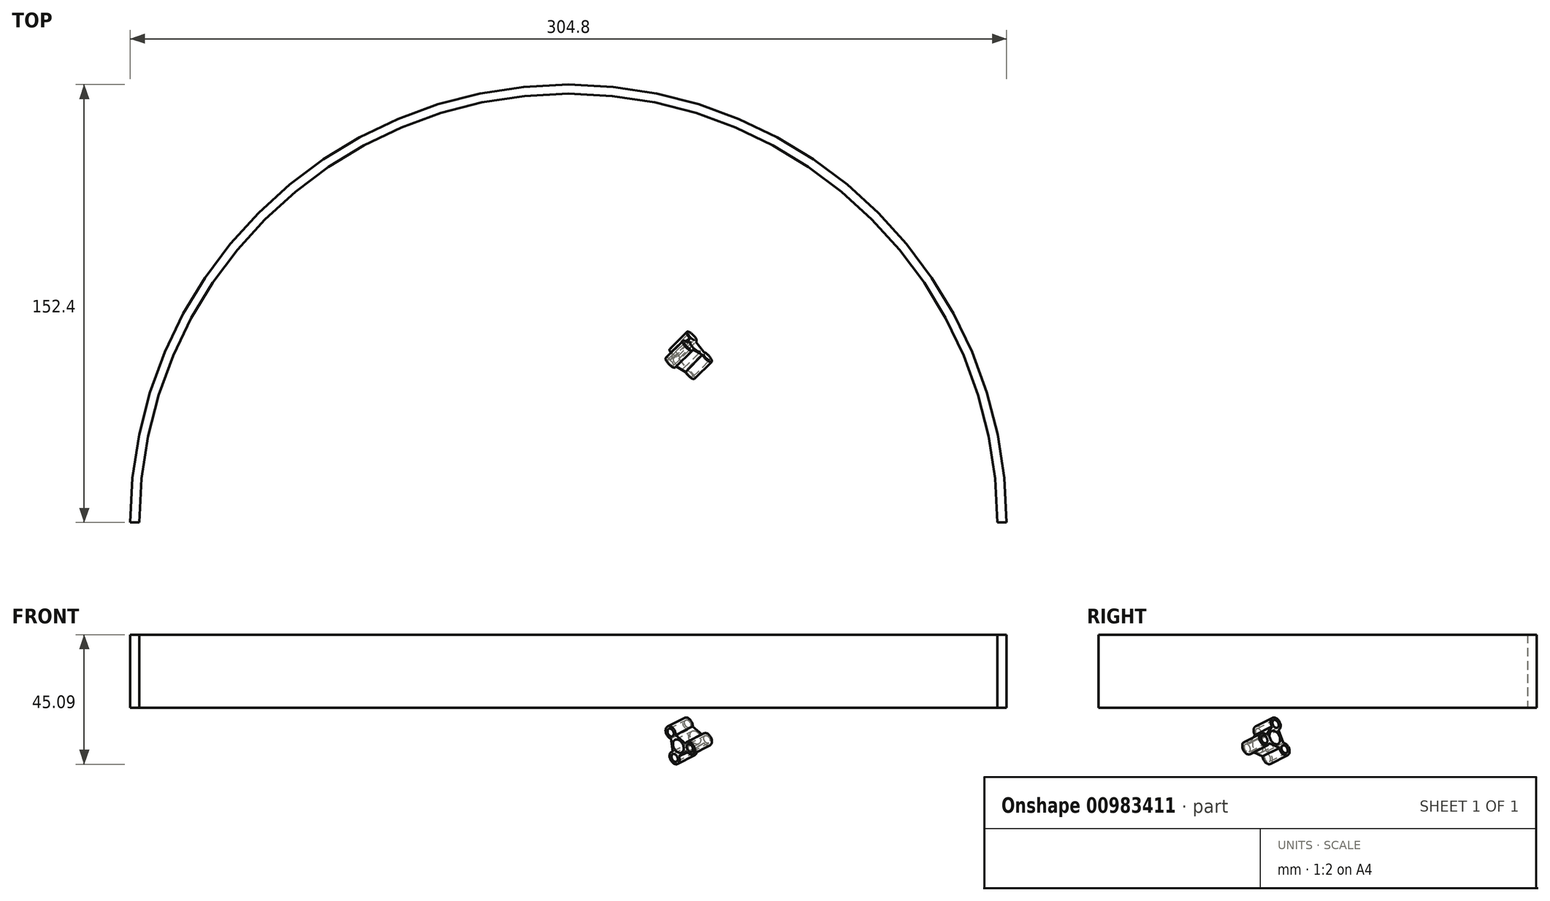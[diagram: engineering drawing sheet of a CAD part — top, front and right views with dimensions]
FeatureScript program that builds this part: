
annotation { "Feature Type Name" : "Feature", "Feature Type Description" : "" }
export const myFeature = defineFeature(function(context is Context, id is Id, definition is map)
    precondition{}
    {
        {
            var Q0;
            Q0=qCreatedBy(makeId("Top.planeOp"),FACE);
            var sketch = newSketch(context, id + "F0", { "sketchPlane" : qUnion([Q0])});
            skArc(sketch, "E0", {"start": v(139.7, 0) * mm, "mid": v(0, 139.7) * mm, "end": v(-139.7, 0) * mm, "construction": true});
            skArc(sketch, "E1", {"start": v(152.4, 0) * mm, "mid": v(0, 152.4) * mm, "end": v(-152.4, 0) * mm});
            skLineSegment(sketch, "E2", {"start": v(0, 0) * mm, "end": v(-209.94, 0) * mm, "construction": true});
            skLineSegment(sketch, "E3", {"start": v(0, 0) * mm, "end": v(212.99, 0) * mm, "construction": true});
            skArc(sketch, "E4.0", {"start": v(15.22, 0.84) * mm, "mid": v(0, 15.24) * mm, "end": v(-15.22, 0.84) * mm, "construction": true});
            skCircle(sketch, "E5.cCircle", {"center": v(0, 0) * mm, "radius": 12.07 * mm, "construction": true});
            skLineSegment(sketch, "E5.0", {"start": v(0, 12.06) * mm, "end": v(10.45, -6.03) * mm, "construction": true});
            skLineSegment(sketch, "E5.1", {"start": v(10.45, -6.03) * mm, "end": v(-10.45, -6.03) * mm, "construction": true});
            skLineSegment(sketch, "E5.2", {"start": v(-10.45, -6.03) * mm, "end": v(0, 12.07) * mm, "construction": true});
            skCircle(sketch, "E6", {"center": v(0, 12.07) * mm, "radius": 2.38 * mm, "construction": true});
            skCircle(sketch, "E7.1.0", {"center": v(10.45, -6.03) * mm, "radius": 2.38 * mm, "construction": true});
            skCircle(sketch, "E7.2.0", {"center": v(-10.45, -6.03) * mm, "radius": 2.38 * mm, "construction": true});
            skLineSegment(sketch, "E7.anchor2", {"start": v(0, 0) * mm, "end": v(-10.45, -6.03) * mm, "construction": true});
            skLineSegment(sketch, "E8", {"start": v(-2.92, 18.85) * mm, "end": v(-236.4, 252.33) * mm, "construction": true});
            skLineSegment(sketch, "E9.MirrorCS", {"start": v(2.92, 18.85) * mm, "end": v(-2.92, 18.85) * mm, "construction": true});
            skLineSegment(sketch, "E10.MirrorCS", {"start": v(2.92, 18.85) * mm, "end": v(236.4, 252.33) * mm, "construction": true});
            skLineSegment(sketch, "E11", {"start": v(0, 0) * mm, "end": v(0, 38.63) * mm, "construction": true});
            skArc(sketch, "E12", {"start": v(149.23, 0) * mm, "mid": v(0, 149.23) * mm, "end": v(-149.23, 0) * mm});
            skLineSegment(sketch, "E13", {"start": v(-152.4, 0) * mm, "end": v(-149.23, 0) * mm});
            skLineSegment(sketch, "E14", {"start": v(149.23, 0) * mm, "end": v(152.4, 0) * mm});
            skSolve(sketch);
        }
        {
            var Q0;
            Q0=makeQuery(id+"F0.imprint","IMPRINT",FACE,{"disambiguationData":[TD([[makeQuery(id+"F0.imprint","IMPRINT",EDGE,{"derivedFrom":sQuery(id+"F0.wireOp",EDGE,"E1")}),1.0]])]});
            extrude(context, id + "F1", {"entities" : qUnion([Q0]), "depth" : 25.4 * mm, "offsetDistance" : 25.4 * mm});
        }
        {
            var Q0;
            Q0=qCreatedBy(makeId("Top.planeOp"),FACE);
            var Q1;
            Q1=sQuery(id+"F0.wireOp",EDGE,"E9.MirrorCS");
            cPlane(context, id + "F2", {"entities" : qUnion([Q0, Q1]), "cplaneType" : CPlaneType.LINE_ANGLE, "offset" : 25.4 * mm, "angle" : 27 * degree, "oppositeDirection" : true, "width" : 152.4 * mm, "height" : 152.4 * mm});
        }
        {
            var Q0;
            Q0=makeQuery(id+"F1.opExtrude","SWEPT_BODY",BODY,{"disambiguationData":[OSD([sQuery(id+"F0.wireOp",EDGE,"E1"),sQuery(id+"F0.wireOp",EDGE,"E12"),sQuery(id+"F0.wireOp",EDGE,"E13"),sQuery(id+"F0.wireOp",EDGE,"E14")])]});
            var Q1;
            Q1=makeQuery(id+"F1.opExtrude","SWEPT_FACE",FACE,{"disambiguationData":[OSD([sQuery(id+"F0.wireOp",EDGE,"E1")])]});
            transform(context, id + "F3", {"entities" : qUnion([Q0]), "transformType" : TransformType.TRANSLATION_DISTANCE, "transformDirection" : qUnion([Q1]), "distance" : 40.13 * mm, "oppositeDirection" : true, "makeCopy" : false});
        }
        {
            var Q0;
            Q0=sQuery(id+"F0.wireOp",EDGE,"E10.MirrorCS");
            cPlane(context, id + "F4", {"entities" : qUnion([Q0]), "cplaneType" : CPlaneType.LINE_ANGLE, "offset" : 25.4 * mm, "angle" : 90 * degree, "width" : 152.4 * mm, "height" : 152.4 * mm});
        }
        {
            var Q0;
            Q0=qCreatedBy(id+"F2.planeOp",FACE);
            var sketch = newSketch(context, id + "F5", { "sketchPlane" : qUnion([Q0])});
            skLineSegment(sketch, "E15", {"start": v(48.51, -67.96) * mm, "end": v(101.32, -127.23) * mm, "construction": true});
            skSolve(sketch);
        }
        {
            var Q0;
            Q0=sQuery(id+"F5.wireOp",VERTEX,"E15.start");
            var Q1;
            Q1=sQuery(id+"F5.wireOp",EDGE,"E15");
            cPlane(context, id + "F6", {"entities" : qUnion([Q0, Q1]), "cplaneType" : CPlaneType.LINE_POINT, "offset" : 25.4 * mm, "width" : 152.4 * mm, "height" : 152.4 * mm});
        }
        {
            var Q0;
            Q0=qCreatedBy(id+"F6.planeOp",FACE);
            var sketch = newSketch(context, id + "F7", { "sketchPlane" : qUnion([Q0])});
            skCircle(sketch, "E16", {"center": v(14.1, -6.5) * mm, "radius": 2.35 * mm});
            skCircle(sketch, "E17.1.0", {"center": v(15.94, 2.78) * mm, "radius": 2.35 * mm});
            skCircle(sketch, "E17.2.0", {"center": v(6.98, -0.26) * mm, "radius": 2.35 * mm});
            skPoint(sketch, "E17.center", {"position": v(12.34, -1.33) * mm});
            skPoint(sketch, "E18.end.orphan", {"position": v(13.29, -4.3) * mm});
            skPoint(sketch, "E19.start.orphan", {"position": v(15.57, 4.29) * mm});
            skCircle(sketch, "E20", {"center": v(12.34, -1.33) * mm, "radius": 2.49 * mm});
            skCircle(sketch, "E21", {"center": v(14.1, -6.5) * mm, "radius": 1.46 * mm});
            skCircle(sketch, "E22.1.0", {"center": v(15.94, 2.78) * mm, "radius": 1.46 * mm});
            skCircle(sketch, "E22.2.0", {"center": v(6.99, -0.26) * mm, "radius": 1.46 * mm});
            skCircle(sketch, "E23.cCircle", {"center": v(12.34, -1.33) * mm, "radius": 3.18 * mm, "construction": true});
            skPoint(sketch, "E23.0.midPoint", {"position": v(11.25, 1.66) * mm});
            skLineSegment(sketch, "E24", {"start": v(13.6, 2.51) * mm, "end": v(9.05, 0.86) * mm});
            skLineSegment(sketch, "E25", {"start": v(15.03, -4.34) * mm, "end": v(15.87, 0.43) * mm});
            skLineSegment(sketch, "E26", {"start": v(12.1, -5.26) * mm, "end": v(8.38, -2.15) * mm});
            skLineSegment(sketch, "E27", {"start": v(12.34, -1.33) * mm, "end": v(14.88, -8.83) * mm, "construction": true});
            skLineSegment(sketch, "E28.0", {"start": v(7.3, -0.02) * mm, "end": v(7.3, -0.02) * mm});
            skLineSegment(sketch, "E28.1", {"start": v(12.34, -1.33) * mm, "end": v(14.1, -6.5) * mm, "construction": true});
            skLineSegment(sketch, "E28.8", {"start": v(7.3, -0.02) * mm, "end": v(7.3, -0.02) * mm});
            skLineSegment(sketch, "E28.9", {"start": v(12.23, -1.37) * mm, "end": v(14.1, -6.5) * mm, "construction": true});
            skLineSegment(sketch, "E29.0", {"start": v(11.25, 1.66) * mm, "end": v(9.05, 0.86) * mm, "construction": true});
            skLineSegment(sketch, "E30.0", {"start": v(13.29, -4.3) * mm, "end": v(14.1, -6.5) * mm, "construction": true});
            skLineSegment(sketch, "E31.0", {"start": v(11.25, 1.66) * mm, "end": v(12.34, -1.33) * mm, "construction": true});
            skSolve(sketch);
        }
        {
            var Q0;
            Q0=makeQuery(id+"F7.imprint","IMPRINT",FACE,{"disambiguationData":[TD([[makeQuery(id+"F7.imprint","IMPRINT",EDGE,{"derivedFrom":sQuery(id+"F7.wireOp",EDGE,"E20")}),-1.0]])]});
            var Q1;
            Q1=makeQuery(id+"F7.imprint","IMPRINT",FACE,{"disambiguationData":[TD([[makeQuery(id+"F7.imprint","IMPRINT",EDGE,{"derivedFrom":sQuery(id+"F7.wireOp",EDGE,"E22.1.0")}),-1.0]])]});
            var Q2;
            Q2=makeQuery(id+"F7.imprint","IMPRINT",FACE,{"disambiguationData":[TD([[makeQuery(id+"F7.imprint","IMPRINT",EDGE,{"derivedFrom":sQuery(id+"F7.wireOp",EDGE,"E22.2.0")}),-1.0]])]});
            var Q3;
            Q3=makeQuery(id+"F7.imprint","IMPRINT",FACE,{"disambiguationData":[TD([[makeQuery(id+"F7.imprint","IMPRINT",EDGE,{"derivedFrom":sQuery(id+"F7.wireOp",EDGE,"E21")}),-1.0]])]});
            extrude(context, id + "F8", {"entities" : qUnion([Q0, Q1, Q2, Q3]), "operationType" : NewBodyOperationType.ADD, "oppositeDirection" : true, "depth" : 11.68 * mm, "offsetDistance" : 25.4 * mm, "hasSecondDirection" : true, "secondDirectionOppositeDirection" : true, "secondDirectionDepth" : 2.8 * mm});
        }
    });
